# Revit family: Plymold-Essentials-Table_Top-Square+
name_source: partatom
category: Furniture
units: mm (PartAtom-declared; Revit-internal decimal feet)

## family parameters
Always vertical = Yes
Cut with Voids When Loaded = No
OmniClass Number = 23.40.20.00
OmniClass Title = General Furniture and Specialties
Render Appearance Source = Family Geometry
Room Calculation Point = No
Shared = No
Work Plane-Based = No

## types (15) — shared parameters
Assembly Code = E2020200
Default Elevation = 0"
Keynote = 12500
Manufacturer = Plymold
Product Documentation Link = https://plymold.com
Revit Model Built By = https://www.servex-us.com
Sustainability = https://plymold.com
TOP EDGE MATERIAL = PLY - Plastic Black
TOP MATERIAL = PLY - Wood Mahogany
Type Comments = Table Tops & Bases
URL = https://plymold.com
zero-valued in all types: Cost

## per-type parameters (varying)
| type | Brand | DE | Depth | Description | PVC | TPD | WEB2 | Width |
| 42042WEB2 | Solid Beech Table Top | No | 42" | Solid Beech Wood Table Top Square - 42”W x 42”D x Adjustable Height | No | No | Yes | 42" |
| 36036WEB2 | Solid Beech Table Top | No | 36" | Solid Beech Wood Table Top Square - 36”W x 36”D x Adjustable Height | No | No | Yes | 36" |
| 30030WEB2 | Solid Beech Table Top | No | 30" | Solid Beech Wood Table Top Square - 30”W x 30”D x Adjustable Height | No | No | Yes | 30" |
| 42042PVC | PVC Edge Table Top | No | 42" | PVC Table Top Square - 42”W x 42”D x Adjustable Height | Yes | No | No | 42" |
| 36036PVC | PVC Edge Table Top | No | 36" | PVC Table Top Square - 36”W x 36”D x Adjustable Height | Yes | No | No | 36" |
| 30030PVC | PVC Edge Table Top | No | 30" | PVC Table Top Square - 30”W x 30”D x Adjustable Height | Yes | No | No | 30" |
| 24024PVC | Dur-A-Edge® Table Top | No | 24" | PVC Table Top Square - 24”W x 24”D x Adjustable Height | No | Yes | No | 24" |
| 42042TPD | Dur-A-Edge® Table Top | No | 42" | Thin Profile Dur-a-Edge Table Top Square - 42”W x 42”D x Adjustable Height | No | Yes | No | 42" |
| 36036TPD | Dur-A-Edge® Table Top | No | 36" | Thin Profile Dur-a-Edge Table Top Square - 36”W x 36”D x Adjustable Height | No | Yes | No | 36" |
| 30030TPD | Dur-A-Edge® Table Top | No | 30" | Thin Profile Dur-a-Edge Table Top Square - 30”W x 30”D x Adjustable Height | No | Yes | No | 30" |
| 24024TPD | Dur-A-Edge® Table Top | No | 24" | Thin Profile Dur-a-Edge Table Top Square - 24”W x 24”D x Adjustable Height | No | Yes | No | 24" |
| 42042DE | Dur-A-Edge® Table Top | Yes | 42" | Dur-a-Edge Table Top Square Bullnose - 42”W x 42”D x Adjustable Height | No | No | No | 42" |
| 36036DE | Dur-A-Edge® Table Top | Yes | 36" | Dur-a-Edge Table Top Square Bullnose - 36”W x 36”D x Adjustable Height | No | No | No | 36" |
| 30030DE | Dur-A-Edge® Table Top | Yes | 30" | Dur-a-Edge Table Top Square Bullnose - 30”W x 30”D x Adjustable Height | No | No | No | 30" |
| 24024DE | Dur-A-Edge® Table Top | Yes | 24" | Dur-a-Edge Table Top Square Bullnose - 24”W x 24”D x Adjustable Height | No | No | No | 24" |

note: column(s) folded — value = type name in every type: Model

## geometry (parser evidence)
native form markers: Sweep x3
no freeform markers — native parametric forms only
